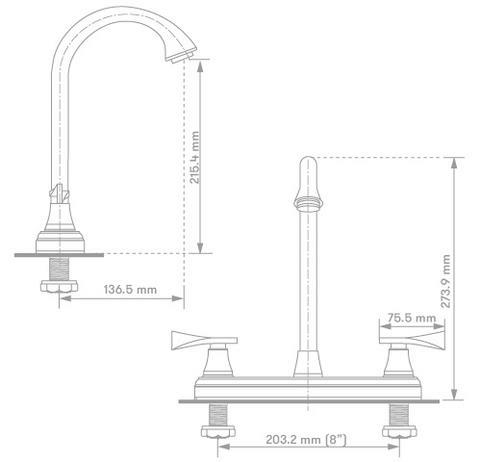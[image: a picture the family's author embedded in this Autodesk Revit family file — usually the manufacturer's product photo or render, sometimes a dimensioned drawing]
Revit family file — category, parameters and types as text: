
# Revit family: 01-2828-11 MEZCLADOR LAVAPLATOS 8 COLECCION PRISTINA
name_source: partatom
category: Aparatos sanitarios
revit_build: Autodesk Revit 2018 (Build: 20170223_1515(x64)
units: mm (PartAtom-declared; Revit-internal decimal feet)

## family parameters
Anfitrión = Cara
Compartido = No
Corte con vacíos al cargar = No
Cota de conector redondo = Diámetro de uso
Número OmniClass = 23.31.11.00
Punto de cálculo de habitación = No
Tipo de pieza = Normal

## types (1)
- 01-2828-11
    Alto Aireador = 215 mm
    Alto brazo = 274 mm  [stored 0.89895 ft]
    Ancho brazo = 137 mm  [stored 0.449475 ft]
    Ancho entre manijas = 203.2 mm  [stored 0.666667 ft]
    Ancho manija = 75 mm
    Conexión AC = Sí
    Conexión AF = Sí
    Conexión de residuos = No
    Conexión de ventilación = No
    Descripción = Bimando
    Elevación por defecto = 0 mm  [stored 0 ft]
    Fabricante = Gricol
    Imagen de tipo = <Ninguno>
    Link Ficha Tecnica = http://infotecnica.gricol.com
    Modelo = 01-2828-11
    Plástico - ABS Cromado = Plastico ABS Cromado
    Product Name = MEZCLADOR LAVAPLATOS 8 COLECCION PRISTINA
    URL = https://www.gricol.com

note: [stored X ft] marks values corroborated as IEEE doubles in the binary element streams (Revit-internal decimal feet)

## geometry (parser evidence)
native form markers: Blend x2, Sweep x4
no freeform markers — native parametric forms only
